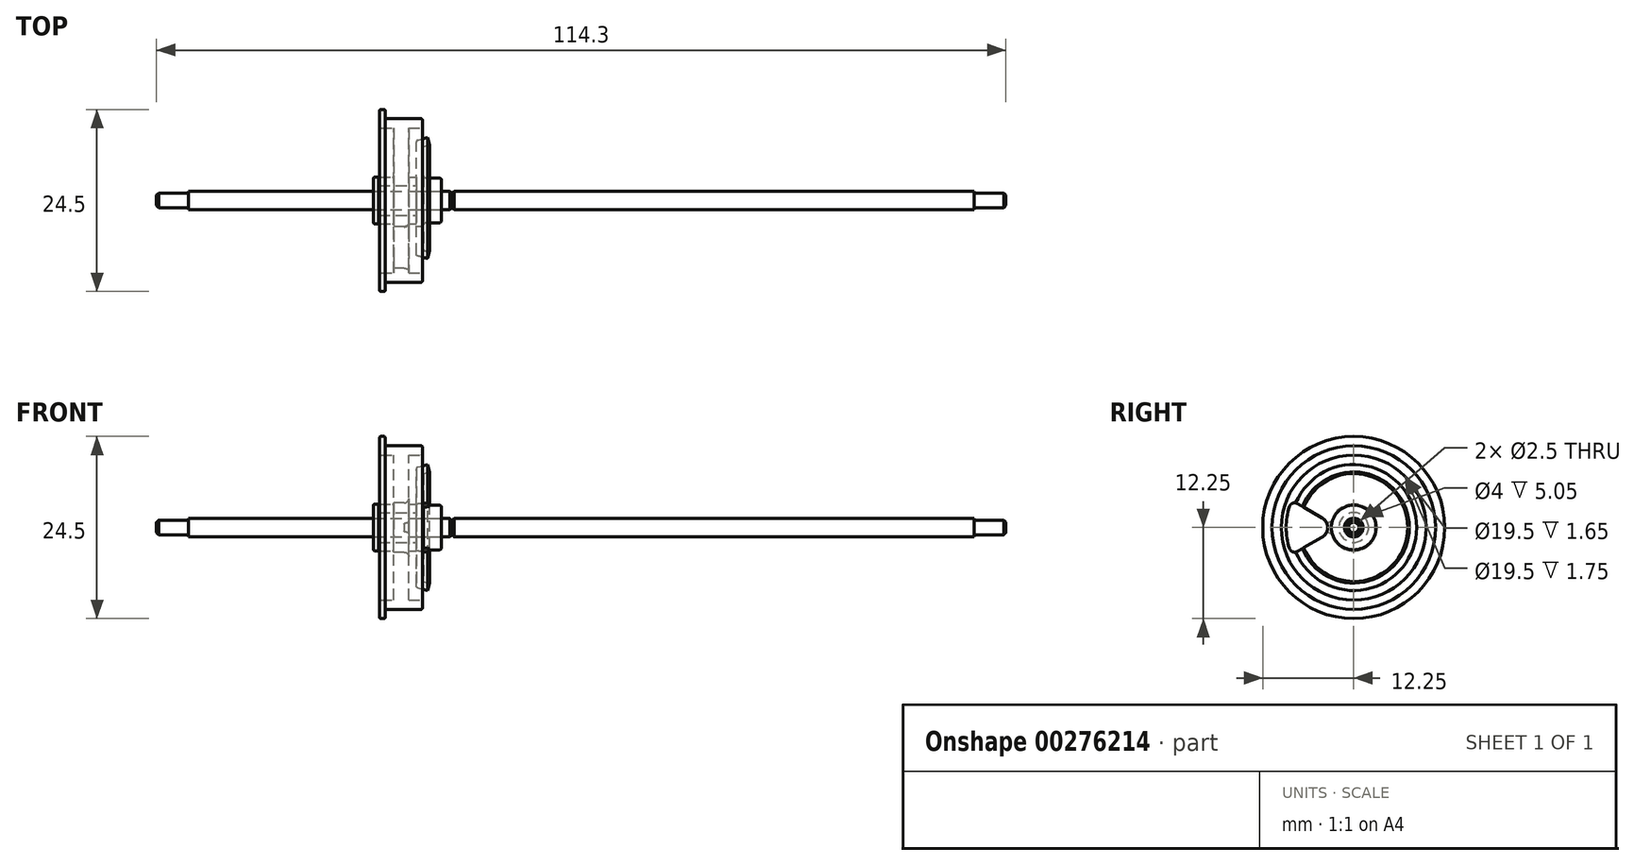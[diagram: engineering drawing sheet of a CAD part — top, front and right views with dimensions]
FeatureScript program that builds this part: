
annotation { "Feature Type Name" : "Feature", "Feature Type Description" : "" }
export const myFeature = defineFeature(function(context is Context, id is Id, definition is map)
    precondition{}
    {
        {
            var Q0;
            Q0=qCreatedBy(makeId("Front.planeOp"),FACE);
            var sketch = newSketch(context, id + "F0", { "sketchPlane" : qUnion([Q0])});
            skLineSegment(sketch, "E0", {"start": v(-163.08, 0) * mm, "end": v(162.95, 0) * mm, "construction": true});
            skLineSegment(sketch, "E1", {"start": v(-17.5, 1.25) * mm, "end": v(-17.5, 0) * mm});
            skLineSegment(sketch, "E2", {"start": v(-17.5, 0) * mm, "end": v(-57.15, 0) * mm});
            skLineSegment(sketch, "E3", {"start": v(-52.85, 1) * mm, "end": v(-52.85, 1.25) * mm});
            skLineSegment(sketch, "E4", {"start": v(-52.85, 1.25) * mm, "end": v(-17.5, 1.25) * mm});
            skLineSegment(sketch, "E5", {"start": v(-17.4, 30.97) * mm, "end": v(-17.4, -21.55) * mm, "construction": true});
            skLineSegment(sketch, "E6.bottom", {"start": v(-17.3, 1.25) * mm, "end": v(52.85, 1.25) * mm});
            skLineSegment(sketch, "E6.left", {"start": v(-17.3, 1.25) * mm, "end": v(-17.3, 0) * mm});
            skLineSegment(sketch, "E6.right", {"start": v(52.85, 1.25) * mm, "end": v(52.85, 1) * mm});
            skLineSegment(sketch, "E7", {"start": v(-52.85, 1) * mm, "end": v(-57.15, 1) * mm});
            skLineSegment(sketch, "E8", {"start": v(-57.15, 1) * mm, "end": v(-57.15, 0) * mm});
            skLineSegment(sketch, "E9", {"start": v(52.85, 1) * mm, "end": v(57.15, 1) * mm});
            skLineSegment(sketch, "E10", {"start": v(57.15, 1) * mm, "end": v(57.15, 0) * mm});
            skLineSegment(sketch, "E11", {"start": v(-17.3, 0) * mm, "end": v(162.95, 0) * mm});
            skLineSegment(sketch, "E12", {"start": v(-18.8, 1.25) * mm, "end": v(-18.8, 3) * mm});
            skLineSegment(sketch, "E13", {"start": v(-18.8, 3) * mm, "end": v(-21.2, 3) * mm});
            skLineSegment(sketch, "E14", {"start": v(-21.2, 3) * mm, "end": v(-21.2, 7.26) * mm});
            skLineSegment(sketch, "E15", {"start": v(-21.2, 7.26) * mm, "end": v(-20.43, 7.47) * mm});
            skLineSegment(sketch, "E16", {"start": v(-20.43, 7.47) * mm, "end": v(-20.66, 8.48) * mm});
            skLineSegment(sketch, "E17", {"start": v(-22.2, 8.07) * mm, "end": v(-22.2, 1.25) * mm});
            skLineSegment(sketch, "E18", {"start": v(-18.7, 0) * mm, "end": v(-20.95, 8.4) * mm, "construction": true});
            skLineSegment(sketch, "E19", {"start": v(-18.7, 1.82) * mm, "end": v(-18.7, -2.88) * mm, "construction": true});
            skLineSegment(sketch, "E20.MirrorCS", {"start": v(-20.7, -8.5) * mm, "end": v(-18.7, 0) * mm, "construction": true});
            skLineSegment(sketch, "E21.MirrorCS", {"start": v(-18.7, 0) * mm, "end": v(-20.95, -8.4) * mm, "construction": true});
            skLineSegment(sketch, "E22", {"start": v(-18.7, 0) * mm, "end": v(-21.29, 8.3) * mm, "construction": true});
            skLineSegment(sketch, "E23", {"start": v(-20.66, 8.48) * mm, "end": v(-22.2, 8.07) * mm});
            skLineSegment(sketch, "E24", {"start": v(-20.66, 8.48) * mm, "end": v(-18.7, 0) * mm, "construction": true});
            skPoint(sketch, "E25", {"position": v(-20.95, 8.4) * mm});
            skPoint(sketch, "E26", {"position": v(-20.68, 7.4) * mm});
            skSolve(sketch);
        }
        {
            var Q0;
            Q0=makeQuery(id+"F0.imprint","IMPRINT",FACE,{"disambiguationData":[TD([[makeQuery(id+"F0.imprint","IMPRINT",EDGE,{"derivedFrom":sQuery(id+"F0.wireOp",EDGE,"E1")}),-1.0]])]});
            var Q1;
            Q1=sQuery(id+"F0.wireOp",EDGE,"E2");
            revolve(context, id + "F1", {"entities" : qUnion([Q0]), "axis" : qUnion([Q1]), "revolveType" : RevolveType.FULL});
        }
        {
            var Q0;
            Q0=makeQuery(id+"F0.imprint","IMPRINT",FACE,{"disambiguationData":[TD([[makeQuery(id+"F0.imprint","IMPRINT",EDGE,{"derivedFrom":sQuery(id+"F0.wireOp",EDGE,"E6.bottom")}),-1.0]])]});
            var Q1;
            {var subQ3=sQuery(id+"F0.wireOp",EDGE,"E1");Q1=makeQuery(id+"F0.imprint","IMPRINT",FACE,{"disambiguationData":[TD([[makeQuery(id+"F0.imprint","IMPRINT",EDGE,{"derivedFrom":subQ3}),-1.0]])]});}
            var Q2;
            Q2 = qConstructionFilter(qBodyType(qCreatedBy(id + "F0" ,EDGE), BodyType.WIRE), ConstructionObject.NO);
            var Q3;
            Q3=sQuery(id+"F0.wireOp",EDGE,"E11");
            revolve(context, id + "F2", {"operationType" : NewBodyOperationType.ADD, "entities" : qUnion([Q0, Q1]), "surfaceEntities" : qUnion([Q2]), "axis" : qUnion([Q3]), "revolveType" : RevolveType.FULL});
        }
        {
            var Q0;
            {var subQ0=sQuery(id+"F0.wireOp",EDGE,"E12");Q0=makeQuery(id+"F0.imprint","IMPRINT",FACE,{"disambiguationData":[TD([[makeQuery(id+"F0.imprint","IMPRINT",EDGE,{"derivedFrom":subQ0}),1.0]])]});}
            var Q1;
            Q1=sQuery(id+"F0.wireOp",EDGE,"E2");
            revolve(context, id + "F3", {"entities" : qUnion([Q0]), "axis" : qUnion([Q1]), "revolveType" : RevolveType.FULL});
        }
        {
            var Q0;
            Q0=makeQuery(id+"F2.opRevolve","SWEPT_EDGE",EDGE,{"disambiguationData":[OSD([sQuery(id+"F0.wireOp",EDGE,"E6.bottom"),sQuery(id+"F0.wireOp",EDGE,"E6.left")])]});
            var Q1;
            Q1=makeQuery(id+"F1.opRevolve","SWEPT_EDGE",EDGE,{"disambiguationData":[OSD([sQuery(id+"F0.wireOp",EDGE,"E1"),sQuery(id+"F0.wireOp",EDGE,"E4")])]});
            chamfer(context, id + "F4", {"entities" : qUnion([Q0, Q1]), "width" : .2 * mm, "tangentPropagation" : true});
        }
        {
            var Q0;
            Q0=qCreatedBy(makeId("Front.planeOp"),FACE);
            var sketch = newSketch(context, id + "F5", { "sketchPlane" : qUnion([Q0])});
            skLineSegment(sketch, "E27.0", {"start": v(-17.5, 0) * mm, "end": v(-57.15, 0) * mm, "construction": true});
            skLineSegment(sketch, "E28", {"start": v(-27.95, 1.25) * mm, "end": v(-27.95, 3.15) * mm});
            skLineSegment(sketch, "E29", {"start": v(-27.95, 3.15) * mm, "end": v(-25.2, 3.15) * mm});
            skLineSegment(sketch, "E30", {"start": v(-25.2, 3.15) * mm, "end": v(-25.2, 9.75) * mm});
            skLineSegment(sketch, "E31", {"start": v(-25.2, 9.75) * mm, "end": v(-27.15, 9.75) * mm});
            skLineSegment(sketch, "E32", {"start": v(-27.15, 9.75) * mm, "end": v(-27.15, 11) * mm});
            skLineSegment(sketch, "E33", {"start": v(-26.35, 11) * mm, "end": v(-21.35, 11) * mm});
            skLineSegment(sketch, "E34", {"start": v(-21.35, 11) * mm, "end": v(-21.35, 9.75) * mm});
            skLineSegment(sketch, "E35", {"start": v(-21.35, 9.75) * mm, "end": v(-23.2, 9.75) * mm});
            skLineSegment(sketch, "E36", {"start": v(-23.2, 9.75) * mm, "end": v(-23.2, 3.15) * mm});
            skLineSegment(sketch, "E37", {"start": v(-23.2, 3.15) * mm, "end": v(-22.2, 3.15) * mm});
            skLineSegment(sketch, "E38", {"start": v(-22.2, 3.15) * mm, "end": v(-22.2, 1.25) * mm});
            skLineSegment(sketch, "E39", {"start": v(-22.2, 1.25) * mm, "end": v(-27.95, 1.25) * mm});
            skLineSegment(sketch, "E40", {"start": v(-27.15, 11) * mm, "end": v(-27.15, 12.25) * mm});
            skLineSegment(sketch, "E41", {"start": v(-27.15, 12.25) * mm, "end": v(-26.35, 12.25) * mm});
            skLineSegment(sketch, "E42", {"start": v(-26.35, 12.25) * mm, "end": v(-26.35, 11) * mm});
            skLineSegment(sketch, "E43", {"start": v(-27.25, 3.15) * mm, "end": v(-27.25, 2) * mm});
            skLineSegment(sketch, "E44", {"start": v(-27.25, 2) * mm, "end": v(-22.2, 2) * mm});
            skSolve(sketch);
        }
        {
            var Q0;
            {var subQ3=sQuery(id+"F5.wireOp",EDGE,"E30");Q0=makeQuery(id+"F5.imprint","IMPRINT",FACE,{"disambiguationData":[TD([[makeQuery(id+"F5.imprint","IMPRINT",EDGE,{"derivedFrom":subQ3}),-1.0]])]});}
            var Q1;
            Q1=sQuery(id+"F0.wireOp",EDGE,"E2");
            revolve(context, id + "F6", {"entities" : qUnion([Q0]), "axis" : qUnion([Q1]), "revolveType" : RevolveType.FULL});
        }
        {
            var Q0;
            Q0=makeQuery(id+"F3.opRevolve","SWEPT_EDGE",EDGE,{"disambiguationData":[OSD([sQuery(id+"F0.wireOp",EDGE,"E17"),sQuery(id+"F0.wireOp",EDGE,"E23")])]});
            var Q1;
            Q1=makeQuery(id+"F3.opRevolve","SWEPT_EDGE",EDGE,{"disambiguationData":[OSD([sQuery(id+"F0.wireOp",EDGE,"E12"),sQuery(id+"F0.wireOp",EDGE,"E13")])]});
            var Q2;
            Q2=makeQuery(id+"F3.opRevolve","SWEPT_EDGE",EDGE,{"disambiguationData":[OSD([sQuery(id+"F0.wireOp",EDGE,"E13"),sQuery(id+"F0.wireOp",EDGE,"E14")])]});
            fillet(context, id + "F7", {"entities" : qUnion([Q0, Q1, Q2]), "radius" : .3 * mm, "tangentPropagation" : true, "allowEdgeOverflow" : false});
        }
        {
            var Q0;
            {var subQ4=sQuery(id+"F5.wireOp",EDGE,"E28");Q0=makeQuery(id+"F5.imprint","IMPRINT",FACE,{"disambiguationData":[TD([[makeQuery(id+"F5.imprint","IMPRINT",EDGE,{"derivedFrom":subQ4}),-1.0]])]});}
            var Q1;
            Q1=sQuery(id+"F0.wireOp",EDGE,"E2");
            revolve(context, id + "F8", {"entities" : qUnion([Q0]), "axis" : qUnion([Q1]), "revolveType" : RevolveType.FULL});
        }
        {
            var Q0;
            Q0=makeQuery(id+"F6.opRevolve","SWEPT_EDGE",EDGE,{"disambiguationData":[OSD([sQuery(id+"F5.wireOp",EDGE,"E29"),sQuery(id+"F5.wireOp",EDGE,"E30")])]});
            var Q1;
            Q1=makeQuery(id+"F6.opRevolve","SWEPT_EDGE",EDGE,{"disambiguationData":[OSD([sQuery(id+"F5.wireOp",EDGE,"E40"),sQuery(id+"F5.wireOp",EDGE,"E41")])]});
            var Q2;
            Q2=makeQuery(id+"F6.opRevolve","SWEPT_EDGE",EDGE,{"disambiguationData":[OSD([sQuery(id+"F5.wireOp",EDGE,"E41"),sQuery(id+"F5.wireOp",EDGE,"E42")])]});
            var Q3;
            Q3=makeQuery(id+"F6.opRevolve","SWEPT_EDGE",EDGE,{"disambiguationData":[OSD([sQuery(id+"F5.wireOp",EDGE,"E33"),sQuery(id+"F5.wireOp",EDGE,"E42")])]});
            var Q4;
            Q4=makeQuery(id+"F6.opRevolve","SWEPT_FACE",FACE,{"disambiguationData":[OSD([sQuery(id+"F5.wireOp",EDGE,"E32"),sQuery(id+"F5.wireOp",EDGE,"E40")])]});
            var Q5;
            Q5=makeQuery(id+"F6.opRevolve","SWEPT_EDGE",EDGE,{"disambiguationData":[OSD([sQuery(id+"F5.wireOp",EDGE,"E34"),sQuery(id+"F5.wireOp",EDGE,"E35")])]});
            var Q6;
            Q6=makeQuery(id+"F6.opRevolve","SWEPT_EDGE",EDGE,{"disambiguationData":[OSD([sQuery(id+"F5.wireOp",EDGE,"E31"),sQuery(id+"F5.wireOp",EDGE,"E32")])]});
            var Q7;
            Q7=makeQuery(id+"F6.opRevolve","SWEPT_EDGE",EDGE,{"disambiguationData":[OSD([sQuery(id+"F5.wireOp",EDGE,"E33"),sQuery(id+"F5.wireOp",EDGE,"E34")])]});
            var Q8;
            Q8=makeQuery(id+"F8.opRevolve","SWEPT_EDGE",EDGE,{"disambiguationData":[OSD([sQuery(id+"F5.wireOp",EDGE,"E28"),sQuery(id+"F5.wireOp",EDGE,"E29")])]});
            fillet(context, id + "F9", {"entities" : qUnion([Q0, Q1, Q2, Q3, Q4, Q5, Q6, Q7, Q8]), "radius" : .2 * mm, "allowEdgeOverflow" : false});
        }
        {
            var Q0;
            Q0=makeQuery(id+"F6.opRevolve","SWEPT_FACE",FACE,{"disambiguationData":[OSD([sQuery(id+"F5.wireOp",EDGE,"E30")])]});
            var sketch = newSketch(context, id + "F10", { "sketchPlane" : qUnion([Q0])});
            skLineSegment(sketch, "E45", {"start": v(0, 0) * mm, "end": v(10.6, 6.13) * mm, "construction": true});
            skLineSegment(sketch, "E46", {"start": v(0, 0) * mm, "end": v(10.6, -6.13) * mm, "construction": true});
            skLineSegment(sketch, "E47", {"start": v(7.57, 3.22) * mm, "end": v(4.25, 1.3) * mm});
            skLineSegment(sketch, "E48", {"start": v(7.57, -3.22) * mm, "end": v(4.25, -1.3) * mm});
            skArc(sketch, "E49", {"start": v(8.66, 2.8) * mm, "mid": v(9.1, 0) * mm, "end": v(8.66, -2.8) * mm});
            skPoint(sketch, "E50.visualSharp", {"position": v(8.33, 3.66) * mm});
            skArc(sketch, "E50.filletArc", {"start": v(8.66, 2.8) * mm, "mid": v(8.22, 3.27) * mm, "end": v(7.57, 3.22) * mm});
            skPoint(sketch, "E51.visualSharp", {"position": v(8.33, -3.66) * mm});
            skArc(sketch, "E51.filletArc", {"start": v(7.57, -3.22) * mm, "mid": v(8.22, -3.27) * mm, "end": v(8.66, -2.8) * mm});
            skPoint(sketch, "E52.visualSharp", {"position": v(2, 0) * mm});
            skArc(sketch, "E52.filletArc", {"start": v(4.25, 1.3) * mm, "mid": v(3.5, 0) * mm, "end": v(4.25, -1.3) * mm});
            skSolve(sketch);
        }
        {
            var Q0;
            Q0 = qSketchRegion(id + "F10", true);
            extrude(context, id + "F11", {"entities" : qUnion([Q0]), "operationType" : NewBodyOperationType.REMOVE, "endBound" : BoundingType.THROUGH_ALL, "oppositeDirection" : true, "depth" : 25 * mm});
        }
        {
            var Q0;
            Q0=makeQuery(id+"F11.boolean.opBoolean","COPY",EDGE,{"derivedFrom":makeQuery(id+"F11.opExtrude","CAP_EDGE",EDGE,{"disambiguationData":[OSD([sQuery(id+"F10.wireOp",EDGE,"E47")])],"isStart":true})});
            var Q1;
            Q1=makeQuery(id+"F11.boolean.opBoolean","INTERSECT",EDGE,{"derivedFrom":[makeQuery(id+"F6.opRevolve","SWEPT_FACE",FACE,{"disambiguationData":[OSD([sQuery(id+"F5.wireOp",EDGE,"E36")])]}),makeQuery(id+"F11.opExtrude","SWEPT_FACE",FACE,{"disambiguationData":[OSD([sQuery(id+"F10.wireOp",EDGE,"E48")])]})]});
            fillet(context, id + "F12", {"entities" : qUnion([Q0, Q1]), "radius" : .6 * mm, "tangentPropagation" : true, "allowEdgeOverflow" : false});
        }
        {
            var Q0;
            Q0=makeQuery(id+"F1.opRevolve","SWEPT_EDGE",EDGE,{"disambiguationData":[OSD([sQuery(id+"F0.wireOp",EDGE,"E7"),sQuery(id+"F0.wireOp",EDGE,"E8")])]});
            var Q1;
            Q1=makeQuery(id+"F2.opRevolve","SWEPT_EDGE",EDGE,{"disambiguationData":[OSD([sQuery(id+"F0.wireOp",EDGE,"E9"),sQuery(id+"F0.wireOp",EDGE,"E10")])]});
            chamfer(context, id + "F13", {"entities" : qUnion([Q0, Q1]), "width" : .3 * mm, "tangentPropagation" : true});
        }
    });
